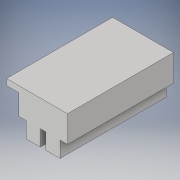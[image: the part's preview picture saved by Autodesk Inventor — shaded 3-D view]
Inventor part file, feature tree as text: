
AUTODESK INVENTOR PART (.ipt)
format: ipt  version: 2019 (Build 230136000, 136)  size: 107,520 bytes
history: native  units: in
note: dims shown in document units (in); Inventor stores cm internally (conversion verified against a paired STEP export)
features: extrude x1, sketch x1
ambient origin geometry x8: Origin, YZ Plane, XZ Plane, XY Plane, X Axis, Y Axis, Z Axis, Center Point
bodies: Solid1 (feature_tree)
feature tree (2):
  extrude  "Extrusion1"  Depth=1.9685in
  sketch  "Sketch1"  dims[d0=3.622in d1=1.9685in d2=0.9055in d3=1.063in d4=1.063in d5=1.1811in d6=0.5512in d7=0.5512in d8=0.3937in d9=7.874in d10=0.0in]
